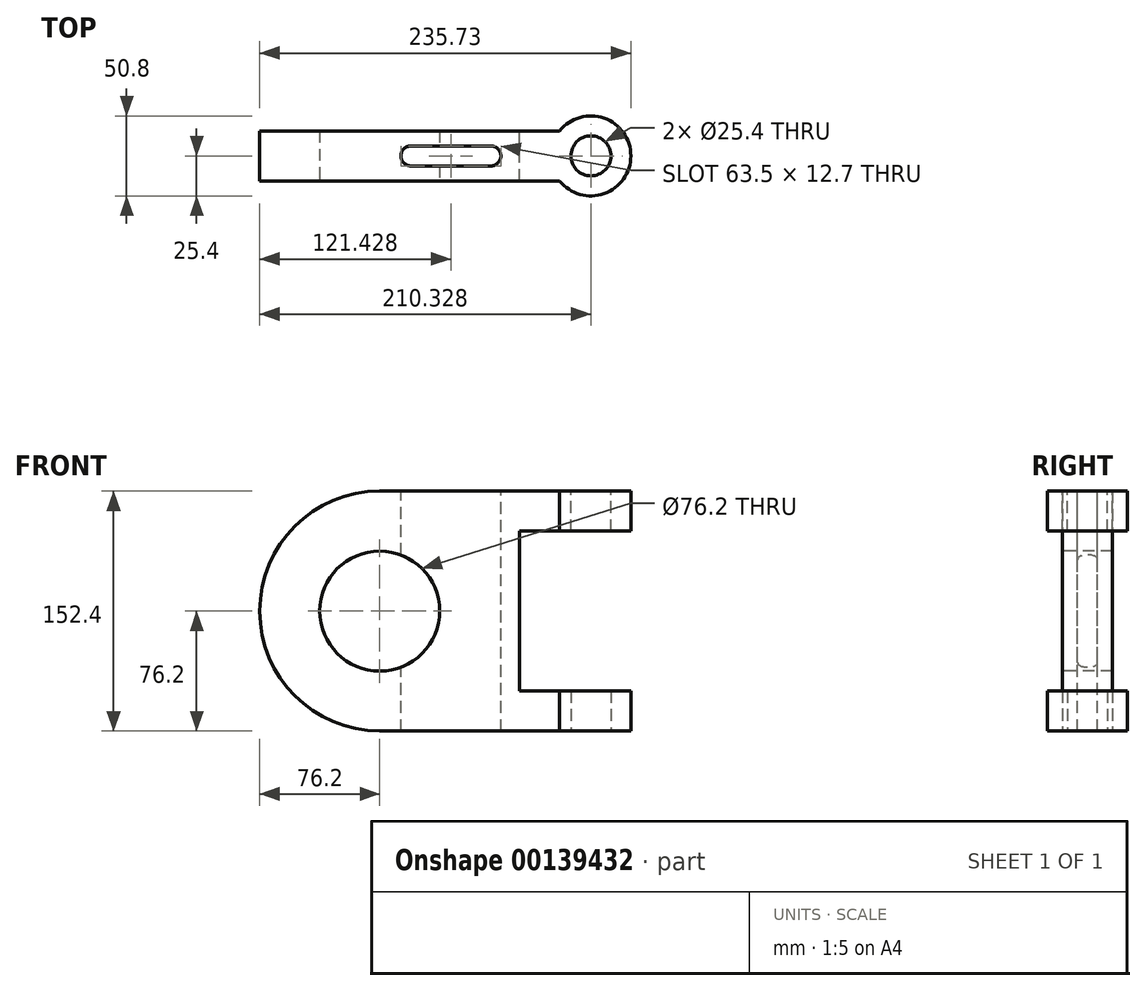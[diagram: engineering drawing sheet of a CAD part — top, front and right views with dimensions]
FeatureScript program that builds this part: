
annotation { "Feature Type Name" : "Feature", "Feature Type Description" : "" }
export const myFeature = defineFeature(function(context is Context, id is Id, definition is map)
    precondition{}
    {
        {
            var Q0;
            Q0=qCreatedBy(makeId("Front.planeOp"),FACE);
            var sketch = newSketch(context, id + "F0", { "sketchPlane" : qUnion([Q0])});
            skArc(sketch, "E0", {"start": v(0, 76.2) * mm, "mid": v(-76.2, 0) * mm, "end": v(0, -76.2) * mm});
            skLineSegment(sketch, "E1", {"start": v(0, 76.2) * mm, "end": v(88.9, 76.2) * mm});
            skLineSegment(sketch, "E2", {"start": v(0, -76.2) * mm, "end": v(88.9, -76.2) * mm});
            skLineSegment(sketch, "E3", {"start": v(88.9, -76.2) * mm, "end": v(88.9, 76.2) * mm});
            skSolve(sketch);
        }
        {
            var Q0;
            Q0 = qSketchRegion(id + "F0", true);
            extrude(context, id + "F1", {"entities" : qUnion([Q0]), "endBound" : BoundingType.SYMMETRIC, "depth" : 31.75 * mm});
        }
        {
            var Q0;
            Q0=makeQuery(id+"F1.opExtrude","CAP_FACE",FACE,{"disambiguationData":[OSD([sQuery(id+"F0.wireOp",EDGE,"E0"),sQuery(id+"F0.wireOp",EDGE,"E1"),sQuery(id+"F0.wireOp",EDGE,"E2"),sQuery(id+"F0.wireOp",EDGE,"h60YZPak-JAec-Qjk4-JqON-mEytXkZMfeVE"),sQuery(id+"F0.wireOp",EDGE,"oelQ9bOs-INgk-ZY3x-7Jw5-m5SkcSD4Kgd5"),sQuery(id+"F0.wireOp",EDGE,"gvpOBRVM-xn1m-BPMr-yWEj-eBoDq50006hO"),sQuery(id+"F0.wireOp",EDGE,"PIiyKdnG-Szu0-BPTW-uEWC-pn33zhNv9d4w"),sQuery(id+"F0.wireOp",EDGE,"kmIJSbh1-RW8B-Aa1Z-YRsj-54L0wzZ1hT5q")])],"isStart":false});
            var sketch = newSketch(context, id + "F2", { "sketchPlane" : qUnion([Q0])});
            skCircle(sketch, "E4", {"center": v(0, 0) * mm, "radius": 38.1 * mm});
            skSolve(sketch);
        }
        {
            var Q0;
            Q0=makeQuery(id+"F2.imprint","IMPRINT",FACE,{"disambiguationData":[TD([[makeQuery(id+"F2.imprint","IMPRINT",EDGE,{"derivedFrom":sQuery(id+"F2.wireOp",EDGE,"E4")}),1.0]])]});
            extrude(context, id + "F3", {"entities" : qUnion([Q0]), "operationType" : NewBodyOperationType.REMOVE, "endBound" : BoundingType.THROUGH_ALL, "oppositeDirection" : true, "depth" : 25.4 * mm});
        }
        {
            var Q0;
            Q0=makeQuery(id+"F1.opExtrude","SWEPT_FACE",FACE,{"disambiguationData":[OSD([sQuery(id+"F0.wireOp",EDGE,"E1")])]});
            var sketch = newSketch(context, id + "F4", { "sketchPlane" : qUnion([Q0])});
            skLineSegment(sketch, "E5", {"start": v(88.9, 15.88) * mm, "end": v(114.3, 15.88) * mm});
            skLineSegment(sketch, "E6", {"start": v(88.9, -15.88) * mm, "end": v(114.3, -15.88) * mm});
            skCircle(sketch, "E7", {"center": v(134.13, 0) * mm, "radius": 25.4 * mm});
            skPoint(sketch, "E7.centerSnap0", {"position": v(114.3, 0) * mm});
            skSolve(sketch);
        }
        {
            var Q0;
            Q0 = qSketchRegion(id + "F4", true);
            var Q1;
            {var subQ0=sQuery(id+"F4.wireOp",EDGE,"E5");Q1=makeQuery(id+"F4.imprint","IMPRINT",FACE,{"disambiguationData":[TD([[makeQuery(id+"F4.imprint","IMPRINT",EDGE,{"derivedFrom":subQ0}),-1.0]])]});}
            extrude(context, id + "F5", {"entities" : qUnion([Q0, Q1]), "operationType" : NewBodyOperationType.ADD, "oppositeDirection" : true, "depth" : 25.4 * mm});
        }
        {
            var Q0;
            {var subQ0=sQuery(id+"F0.wireOp",EDGE,"E1");Q0=makeQuery(id+"F5.boolean.opBoolean","MERGE",FACE,{"derivedFrom":[makeQuery(id+"F1.opExtrude","SWEPT_FACE",FACE,{"disambiguationData":[OSD([subQ0])]}),makeQuery(id+"F5.opExtrude","CAP_FACE",FACE,{"disambiguationData":[OSD([subQ0,sQuery(id+"F0.wireOp",EDGE,"E3"),sQuery(id+"F4.wireOp",EDGE,"E5"),sQuery(id+"F4.wireOp",EDGE,"E6"),sQuery(id+"F4.wireOp",EDGE,"E7")])],"isStart":true})]});}
            var sketch = newSketch(context, id + "F6", { "sketchPlane" : qUnion([Q0])});
            skCircle(sketch, "E8", {"center": v(134.13, 0) * mm, "radius": 12.7 * mm});
            skSolve(sketch);
        }
        {
            var Q0;
            Q0 = qSketchRegion(id + "F6", true);
            extrude(context, id + "F7", {"entities" : qUnion([Q0]), "operationType" : NewBodyOperationType.REMOVE, "endBound" : BoundingType.THROUGH_ALL, "oppositeDirection" : true, "depth" : 25.4 * mm});
        }
        {
            var Q0;
            Q0=makeQuery(id+"F1.opExtrude","SWEPT_FACE",FACE,{"disambiguationData":[OSD([sQuery(id+"F0.wireOp",EDGE,"E2")])]});
            var sketch = newSketch(context, id + "F8", { "sketchPlane" : qUnion([Q0])});
            skLineSegment(sketch, "E9", {"start": v(88.9, 15.88) * mm, "end": v(114.3, 15.88) * mm});
            skLineSegment(sketch, "E10", {"start": v(88.9, -15.88) * mm, "end": v(114.3, -15.88) * mm});
            skCircle(sketch, "E11", {"center": v(134.13, 0) * mm, "radius": 25.4 * mm});
            skSolve(sketch);
        }
        {
            var Q0;
            {var subQ0=sQuery(id+"F8.wireOp",EDGE,"E9");Q0=makeQuery(id+"F8.imprint","IMPRINT",FACE,{"disambiguationData":[TD([[makeQuery(id+"F8.imprint","IMPRINT",EDGE,{"derivedFrom":subQ0}),-1.0]])]});}
            var Q1;
            {var subQ0=sQuery(id+"F8.wireOp",EDGE,"E11");var subQ1=makeQuery(id+"F8.imprint","INTERSECT",VERTEX,{"derivedFrom":[sQuery(id+"F8.wireOp",EDGE,"E9"),subQ0]});Q1=makeQuery(id+"F8.imprint","IMPRINT",FACE,{"disambiguationData":[TD([[makeQuery(id+"F8.imprint","IMPRINT",EDGE,{"disambiguationData":[TD([[subQ1,-1.0]])],"derivedFrom":subQ0}),1.0]])]});}
            extrude(context, id + "F9", {"entities" : qUnion([Q0, Q1]), "operationType" : NewBodyOperationType.ADD, "oppositeDirection" : true, "depth" : 25.4 * mm});
        }
        {
            var Q0;
            {var subQ0=sQuery(id+"F0.wireOp",EDGE,"E2");Q0=makeQuery(id+"F9.boolean.opBoolean","MERGE",FACE,{"derivedFrom":[makeQuery(id+"F1.opExtrude","SWEPT_FACE",FACE,{"disambiguationData":[OSD([subQ0])]}),makeQuery(id+"F9.opExtrude","CAP_FACE",FACE,{"disambiguationData":[OSD([subQ0,sQuery(id+"F0.wireOp",EDGE,"E3"),sQuery(id+"F8.wireOp",EDGE,"E9"),sQuery(id+"F8.wireOp",EDGE,"E10"),sQuery(id+"F8.wireOp",EDGE,"E11")])],"isStart":true})]});}
            var sketch = newSketch(context, id + "F10", { "sketchPlane" : qUnion([Q0])});
            skCircle(sketch, "E12", {"center": v(134.13, 0) * mm, "radius": 12.7 * mm});
            skSolve(sketch);
        }
        {
            var Q0;
            Q0 = qSketchRegion(id + "F10", true);
            extrude(context, id + "F11", {"entities" : qUnion([Q0]), "operationType" : NewBodyOperationType.REMOVE, "endBound" : BoundingType.THROUGH_ALL, "oppositeDirection" : true, "depth" : 25.4 * mm});
        }
        {
            var Q0;
            {var subQ0=sQuery(id+"F0.wireOp",EDGE,"E1");Q0=makeQuery(id+"F5.boolean.opBoolean","MERGE",FACE,{"derivedFrom":[makeQuery(id+"F1.opExtrude","SWEPT_FACE",FACE,{"disambiguationData":[OSD([subQ0])]}),makeQuery(id+"F5.opExtrude","CAP_FACE",FACE,{"disambiguationData":[OSD([subQ0,sQuery(id+"F0.wireOp",EDGE,"E3"),sQuery(id+"F4.wireOp",EDGE,"E5"),sQuery(id+"F4.wireOp",EDGE,"E6"),sQuery(id+"F4.wireOp",EDGE,"E7")])],"isStart":true})]});}
            var sketch = newSketch(context, id + "F12", { "sketchPlane" : qUnion([Q0])});
            skSolve(sketch);
        }
        {
            var Q0;
            Q0=makeQuery(id+"F12.imprint","IMPRINT",FACE,{"disambiguationData":[TD([[makeQuery(id+"F12.imprint","IMPRINT",EDGE,{"derivedFrom":makeQuery(id+"F5.opExtrude","CAP_EDGE",EDGE,{"disambiguationData":[OSD([sQuery(id+"F4.wireOp",EDGE,"E7")])],"isStart":true})}),1.0]])]});
            var sketch = newSketch(context, id + "F13", { "sketchPlane" : qUnion([Q0])});
            skArc(sketch, "E13", {"start": v(19.83, 6.35) * mm, "mid": v(13.48, 0) * mm, "end": v(19.83, -6.35) * mm});
            skArc(sketch, "E14", {"start": v(70.63, -6.35) * mm, "mid": v(76.98, 0) * mm, "end": v(70.63, 6.35) * mm});
            skLineSegment(sketch, "E15", {"start": v(19.83, 6.35) * mm, "end": v(70.63, 6.35) * mm});
            skLineSegment(sketch, "E16", {"start": v(19.83, -6.35) * mm, "end": v(70.63, -6.35) * mm});
            skSolve(sketch);
        }
        {
            var Q0;
            Q0 = qSketchRegion(id + "F13", true);
            extrude(context, id + "F14", {"entities" : qUnion([Q0]), "operationType" : NewBodyOperationType.REMOVE, "endBound" : BoundingType.THROUGH_ALL, "oppositeDirection" : true, "depth" : 25.4 * mm});
        }
    });
